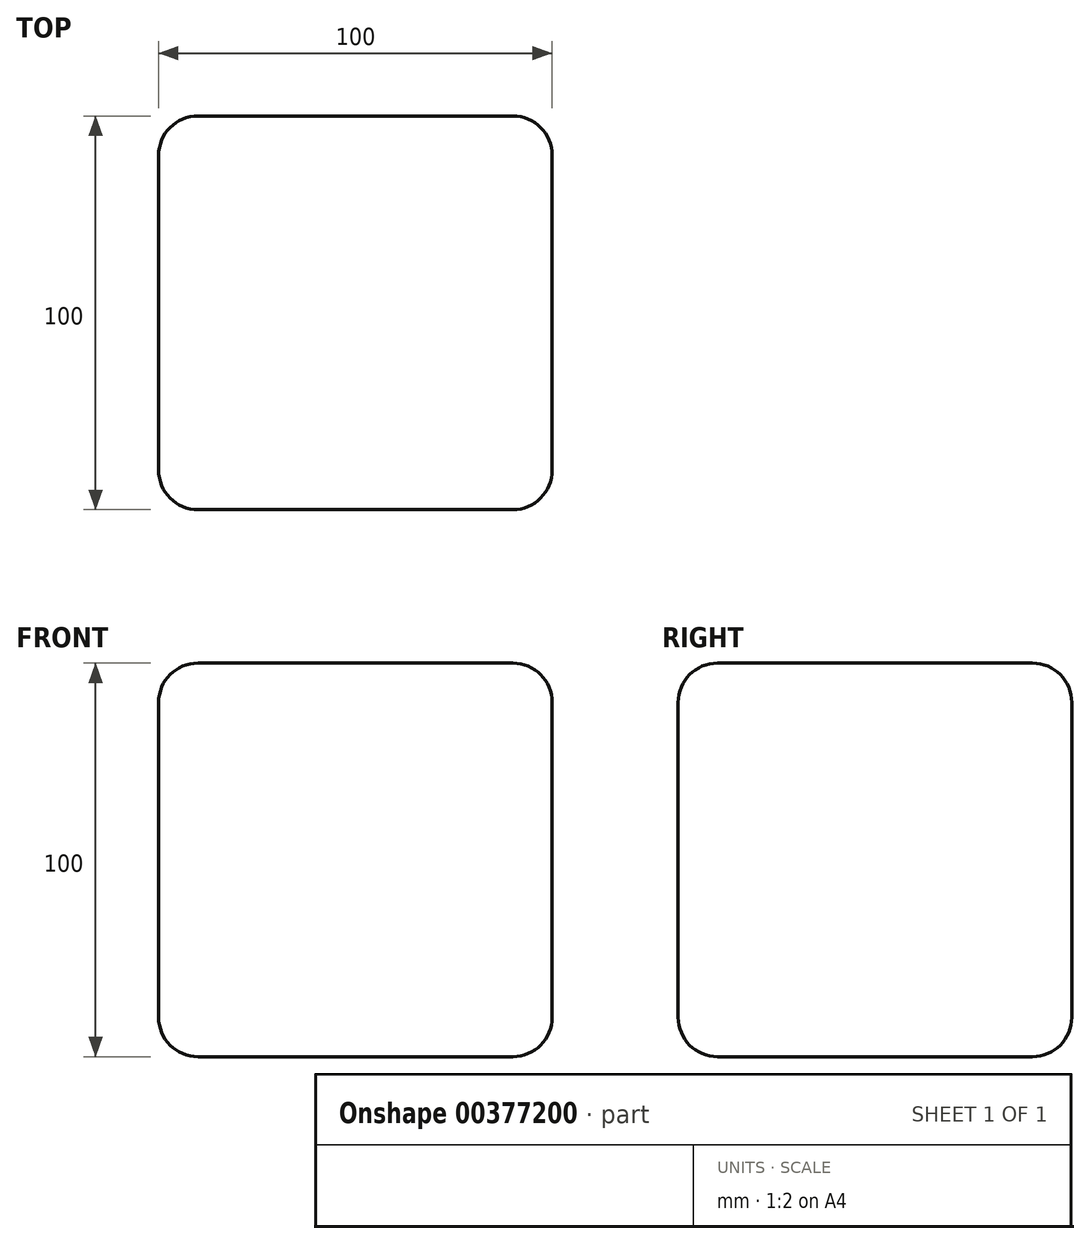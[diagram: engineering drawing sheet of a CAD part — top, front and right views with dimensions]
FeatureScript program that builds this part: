
annotation { "Feature Type Name" : "Feature", "Feature Type Description" : "" }
export const myFeature = defineFeature(function(context is Context, id is Id, definition is map)
    precondition{}
    {
        {
            var Q0;
            Q0=qCreatedBy(makeId("Top.planeOp"),FACE);
            var sketch = newSketch(context, id + "F0", { "sketchPlane" : qUnion([Q0])});
            skLineSegment(sketch, "E0.bottom", {"start": v(50, 50) * mm, "end": v(-50, 50) * mm});
            skLineSegment(sketch, "E0.top", {"start": v(50, -50) * mm, "end": v(-50, -50) * mm});
            skLineSegment(sketch, "E0.left", {"start": v(50, 50) * mm, "end": v(50, -50) * mm});
            skLineSegment(sketch, "E0.right", {"start": v(-50, 50) * mm, "end": v(-50, -50) * mm});
            skPoint(sketch, "E0.middle", {"position": v(0, 0) * mm});
            skSolve(sketch);
        }
        {
            var Q0;
            Q0=makeQuery(id+"F0.imprint","IMPRINT",FACE,{"disambiguationData":[TD([[makeQuery(id+"F0.imprint","IMPRINT",EDGE,{"derivedFrom":sQuery(id+"F0.wireOp",EDGE,"E0.bottom")}),1.0]])]});
            extrude(context, id + "F1", {"entities" : qUnion([Q0]), "depth" : 50 * mm, "hasSecondDirection" : true, "secondDirectionOppositeDirection" : true, "secondDirectionDepth" : 50 * mm});
        }
        {
            var Q0;
            Q0=makeQuery(id+"F1.opExtrude","CAP_FACE",FACE,{"disambiguationData":[OSD([sQuery(id+"F0.wireOp",EDGE,"E0.bottom"),sQuery(id+"F0.wireOp",EDGE,"E0.top"),sQuery(id+"F0.wireOp",EDGE,"E0.left"),sQuery(id+"F0.wireOp",EDGE,"E0.right")])],"isStart":false});
            var Q1;
            Q1=makeQuery(id+"F1.opExtrude","SWEPT_FACE",FACE,{"disambiguationData":[OSD([sQuery(id+"F0.wireOp",EDGE,"E0.top")])]});
            var Q2;
            Q2=makeQuery(id+"F1.opExtrude","SWEPT_FACE",FACE,{"disambiguationData":[OSD([sQuery(id+"F0.wireOp",EDGE,"E0.left")])]});
            var Q3;
            Q3=makeQuery(id+"F1.opExtrude","SWEPT_FACE",FACE,{"disambiguationData":[OSD([sQuery(id+"F0.wireOp",EDGE,"E0.bottom")])]});
            var Q4;
            Q4=makeQuery(id+"F1.opExtrude","CAP_FACE",FACE,{"disambiguationData":[OSD([sQuery(id+"F0.wireOp",EDGE,"E0.bottom"),sQuery(id+"F0.wireOp",EDGE,"E0.top"),sQuery(id+"F0.wireOp",EDGE,"E0.left"),sQuery(id+"F0.wireOp",EDGE,"E0.right")])],"isStart":true});
            var Q5;
            Q5=makeQuery(id+"F1.opExtrude","SWEPT_FACE",FACE,{"disambiguationData":[OSD([sQuery(id+"F0.wireOp",EDGE,"E0.right")])]});
            fillet(context, id + "F2", {"entities" : qUnion([Q0, Q1, Q2, Q3, Q4, Q5]), "radius" : 10 * mm, "tangentPropagation" : true, "allowEdgeOverflow" : false});
        }
    });
